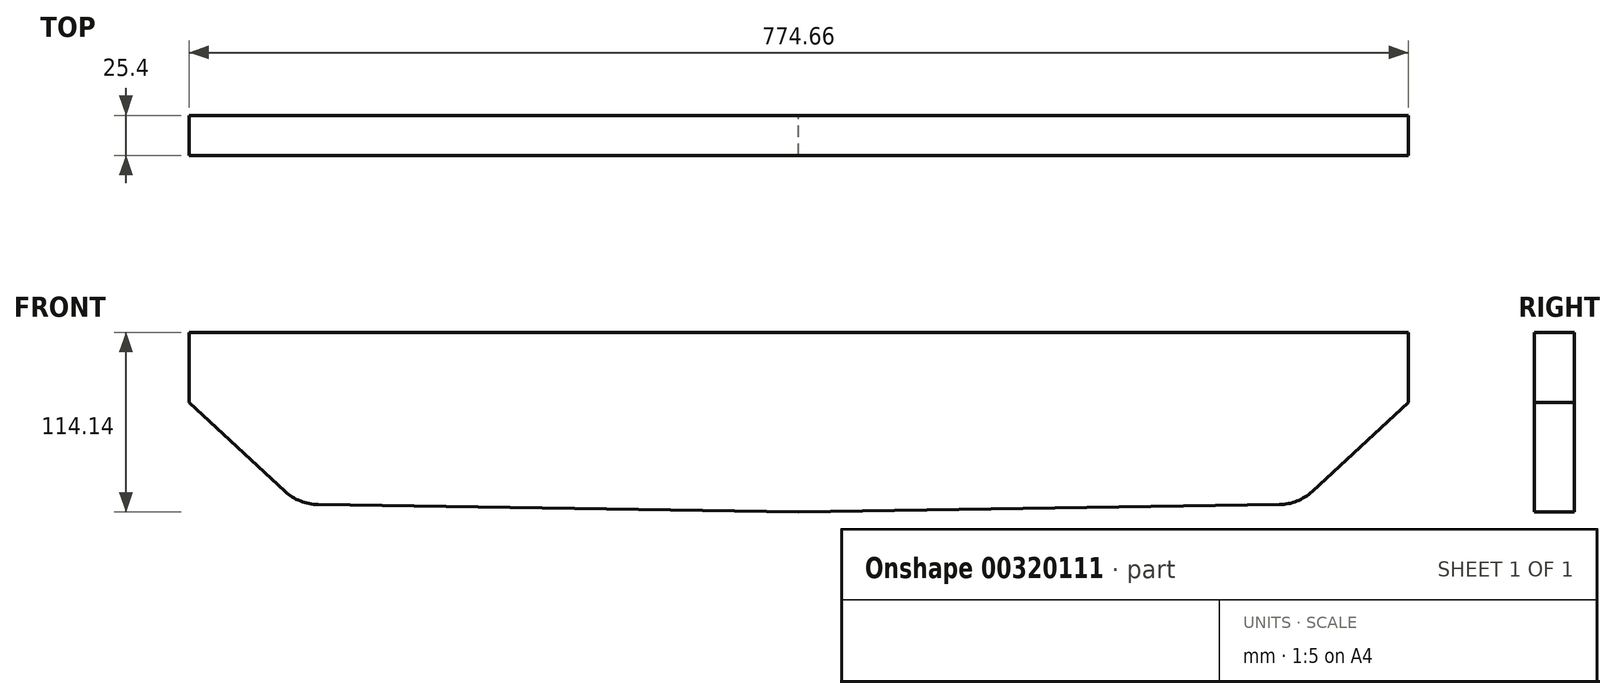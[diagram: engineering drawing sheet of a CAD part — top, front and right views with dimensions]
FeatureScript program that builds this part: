
annotation { "Feature Type Name" : "Feature", "Feature Type Description" : "" }
export const myFeature = defineFeature(function(context is Context, id is Id, definition is map)
    precondition{}
    {
        {
            var Q0;
            Q0=qCreatedBy(makeId("Front.planeOp"),FACE);
            var sketch = newSketch(context, id + "F0", { "sketchPlane" : qUnion([Q0])});
            skCircle(sketch, "E0", {"center": v(0, 0) * mm, "radius": 76.2 * mm, "construction": true});
            skLineSegment(sketch, "E1", {"start": v(-386.5, -76.45) * mm, "end": v(376.46, -75.96) * mm, "construction": true});
            skCircle(sketch, "E2", {"center": v(0, 0) * mm, "radius": 22.24 * mm, "construction": true});
            skCircle(sketch, "E3", {"center": v(-304.76, 4.76) * mm, "radius": 76.2 * mm, "construction": true});
            skCircle(sketch, "E4", {"center": v(304.8, 4.76) * mm, "radius": 76.2 * mm, "construction": true});
            skCircle(sketch, "E5", {"center": v(-304.76, 4.76) * mm, "radius": 22.24 * mm, "construction": true});
            skCircle(sketch, "E6", {"center": v(304.8, 4.76) * mm, "radius": 22.24 * mm, "construction": true});
            skLineSegment(sketch, "E7", {"start": v(-304.42, 27) * mm, "end": v(0, 22.24) * mm, "construction": true});
            skLineSegment(sketch, "E8", {"start": v(-305.11, -17.47) * mm, "end": v(0, -22.24) * mm, "construction": true});
            skLineSegment(sketch, "E9", {"start": v(0, -22.24) * mm, "end": v(305.15, -17.47) * mm, "construction": true});
            skLineSegment(sketch, "E10", {"start": v(0, 22.24) * mm, "end": v(304.45, 27) * mm, "construction": true});
            skLineSegment(sketch, "E11.bottom", {"start": v(-387.31, 82.55) * mm, "end": v(387.35, 82.55) * mm});
            skLineSegment(sketch, "E11.left", {"start": v(-387.31, 82.55) * mm, "end": v(-387.31, 38.1) * mm});
            skLineSegment(sketch, "E11.right", {"start": v(387.35, 82.55) * mm, "end": v(387.35, 38.1) * mm});
            skArc(sketch, "E12", {"start": v(-326.21, -18.42) * mm, "mid": v(-316.5, -24.56) * mm, "end": v(-305.26, -26.82) * mm});
            skCircle(sketch, "E13", {"center": v(0, 0) * mm, "radius": 31.58 * mm, "construction": true});
            skArc(sketch, "E14", {"start": v(305.15, -26.82) * mm, "mid": v(316.48, -24.58) * mm, "end": v(326.25, -18.42) * mm});
            skCircle(sketch, "E15", {"center": v(-304.76, 4.76) * mm, "radius": 25.23 * mm, "construction": true});
            skCircle(sketch, "E16", {"center": v(0, 0) * mm, "radius": 25.23 * mm, "construction": true});
            skCircle(sketch, "E17", {"center": v(304.8, 4.76) * mm, "radius": 25.23 * mm, "construction": true});
            skLineSegment(sketch, "E18", {"start": v(-387.31, 38.1) * mm, "end": v(-326.21, -18.42) * mm});
            skLineSegment(sketch, "E19", {"start": v(387.35, 38.1) * mm, "end": v(326.25, -18.42) * mm});
            skLineSegment(sketch, "E20", {"start": v(-305.26, -26.82) * mm, "end": v(0, -31.59) * mm});
            skLineSegment(sketch, "E21", {"start": v(0, -31.59) * mm, "end": v(305.15, -26.82) * mm});
            skSolve(sketch);
        }
        {
            var Q0;
            Q0 = qSketchRegion(id + "F0", true);
            extrude(context, id + "F1", {"entities" : qUnion([Q0]), "depth" : 25.4 * mm});
        }
    });
